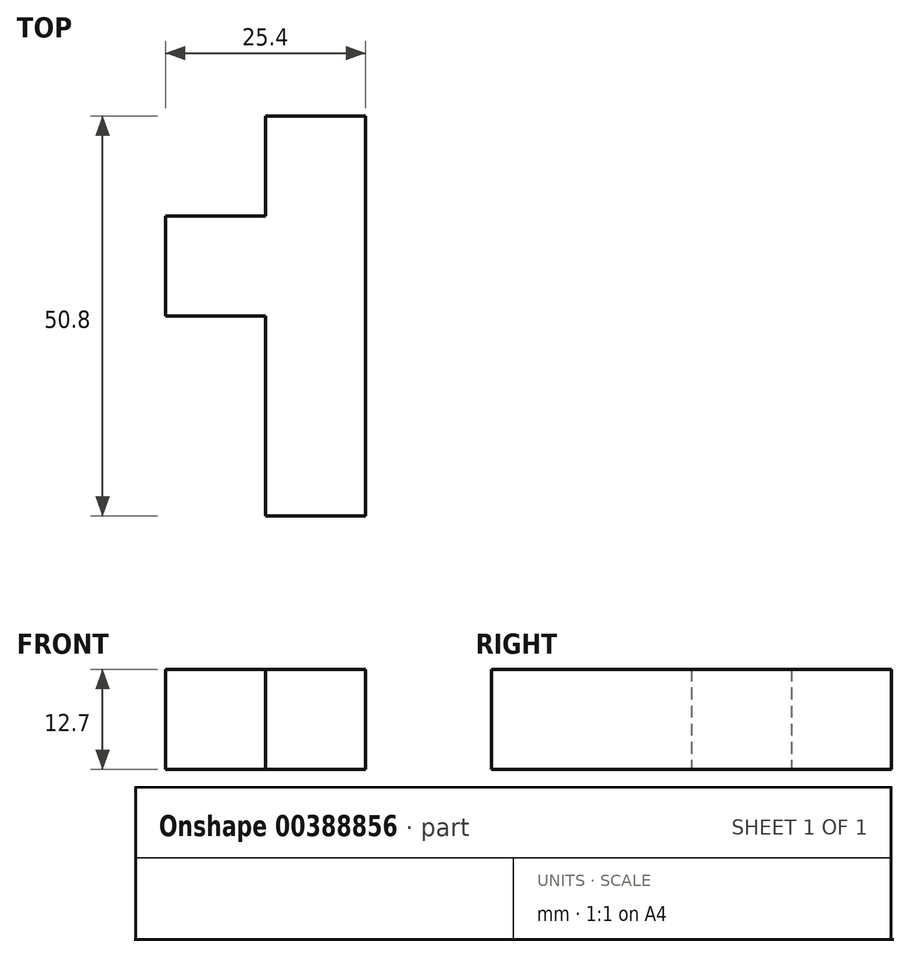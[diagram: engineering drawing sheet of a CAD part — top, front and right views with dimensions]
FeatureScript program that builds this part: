
annotation { "Feature Type Name" : "Feature", "Feature Type Description" : "" }
export const myFeature = defineFeature(function(context is Context, id is Id, definition is map)
    precondition{}
    {
        {
            var Q0;
            Q0=qCreatedBy(makeId("Top.planeOp"),FACE);
            var sketch = newSketch(context, id + "F0", { "sketchPlane" : qUnion([Q0])});
            skLineSegment(sketch, "E0.bottom", {"start": v(0, 0) * mm, "end": v(12.7, 0) * mm});
            skLineSegment(sketch, "E0.top", {"start": v(0, 50.8) * mm, "end": v(12.7, 50.8) * mm});
            skLineSegment(sketch, "E0.right", {"start": v(12.7, 0) * mm, "end": v(12.7, 50.8) * mm});
            skLineSegment(sketch, "E1.bottom", {"start": v(0, 38.1) * mm, "end": v(-12.7, 38.1) * mm});
            skLineSegment(sketch, "E1.top", {"start": v(0, 25.4) * mm, "end": v(-12.7, 25.4) * mm});
            skLineSegment(sketch, "E1.right", {"start": v(-12.7, 38.1) * mm, "end": v(-12.7, 25.4) * mm});
            skLineSegment(sketch, "E2.left", {"start": v(0, 50.8) * mm, "end": v(0, 38.1) * mm});
            skLineSegment(sketch, "E3.trimOffspring", {"start": v(0, 38.1) * mm, "end": v(0, 50.8) * mm});
            skLineSegment(sketch, "E4", {"start": v(0, 25.4) * mm, "end": v(0, 0) * mm});
            skSolve(sketch);
        }
        {
            var Q0;
            Q0=makeQuery(id+"F0.imprint","IMPRINT",FACE,{"disambiguationData":[TD([[makeQuery(id+"F0.imprint","IMPRINT",EDGE,{"derivedFrom":sQuery(id+"F0.wireOp",EDGE,"E0.bottom")}),1.0]])]});
            extrude(context, id + "F1", {"entities" : qUnion([Q0]), "depth" : 12.7 * mm});
        }
    });
